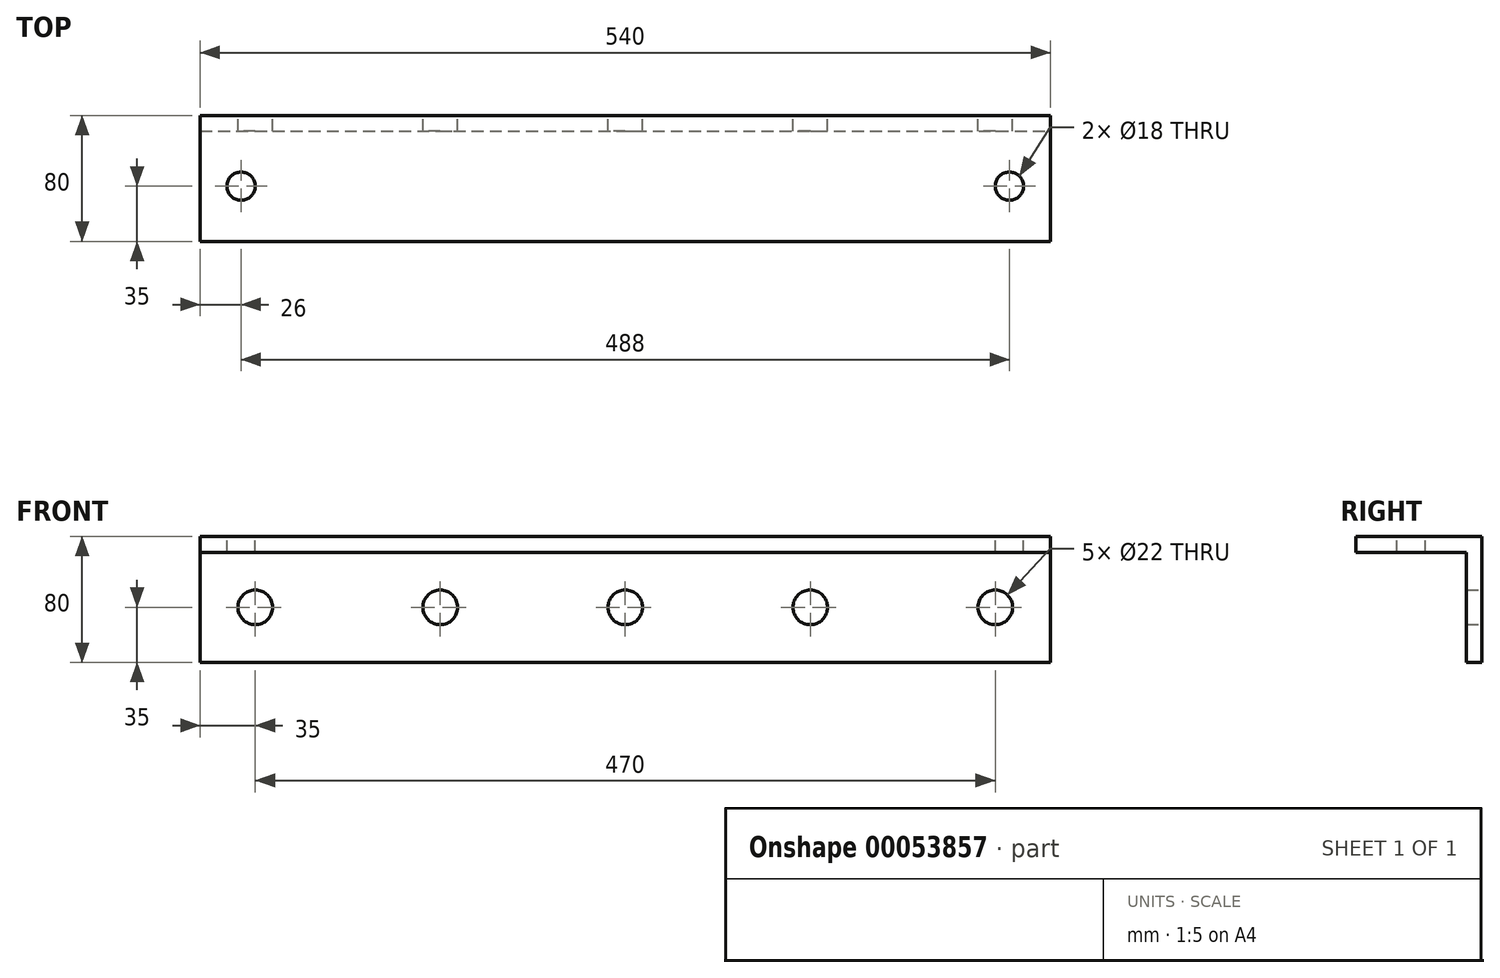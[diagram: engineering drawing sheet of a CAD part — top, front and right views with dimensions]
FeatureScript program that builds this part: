
annotation { "Feature Type Name" : "Feature", "Feature Type Description" : "" }
export const myFeature = defineFeature(function(context is Context, id is Id, definition is map)
    precondition{}
    {
        {
            var Q0;
            Q0=qCreatedBy(makeId("Front.planeOp"),FACE);
            var sketch = newSketch(context, id + "F0", { "sketchPlane" : qUnion([Q0])});
            skLineSegment(sketch, "E0.bottom", {"start": v(0, 0) * mm, "end": v(540, 0) * mm});
            skLineSegment(sketch, "E0.top", {"start": v(0, 80) * mm, "end": v(540, 80) * mm});
            skLineSegment(sketch, "E0.left", {"start": v(0, 0) * mm, "end": v(0, 80) * mm});
            skLineSegment(sketch, "E0.right", {"start": v(540, 0) * mm, "end": v(540, 80) * mm});
            skSolve(sketch);
        }
        {
            var Q0;
            Q0=makeQuery(id+"F0.imprint","IMPRINT",FACE,{"disambiguationData":[TD([[makeQuery(id+"F0.imprint","IMPRINT",EDGE,{"derivedFrom":sQuery(id+"F0.wireOp",EDGE,"E0.bottom")}),1.0]])]});
            extrude(context, id + "F1", {"entities" : qUnion([Q0]), "depth" : 10 * mm});
        }
        {
            var Q0;
            Q0=makeQuery(id+"F1.opExtrude","CAP_FACE",FACE,{"disambiguationData":[OSD([sQuery(id+"F0.wireOp",EDGE,"E0.bottom"),sQuery(id+"F0.wireOp",EDGE,"E0.top"),sQuery(id+"F0.wireOp",EDGE,"E0.left"),sQuery(id+"F0.wireOp",EDGE,"E0.right")])],"isStart":false});
            var sketch = newSketch(context, id + "F2", { "sketchPlane" : qUnion([Q0])});
            skLineSegment(sketch, "E1.bottom", {"start": v(0, 80) * mm, "end": v(540, 80) * mm});
            skLineSegment(sketch, "E1.top", {"start": v(0, 70) * mm, "end": v(540, 70) * mm});
            skLineSegment(sketch, "E1.left", {"start": v(0, 80) * mm, "end": v(0, 70) * mm});
            skLineSegment(sketch, "E1.right", {"start": v(540, 80) * mm, "end": v(540, 70) * mm});
            skSolve(sketch);
        }
        {
            var Q0;
            Q0 = qSketchRegion(id + "F2", true);
            extrude(context, id + "F3", {"entities" : qUnion([Q0]), "operationType" : NewBodyOperationType.ADD, "depth" : 70 * mm});
        }
        {
            var Q0;
            Q0=makeQuery(id+"F1.opExtrude","CAP_FACE",FACE,{"disambiguationData":[OSD([sQuery(id+"F0.wireOp",EDGE,"E0.bottom"),sQuery(id+"F0.wireOp",EDGE,"E0.top"),sQuery(id+"F0.wireOp",EDGE,"E0.left"),sQuery(id+"F0.wireOp",EDGE,"E0.right")])],"isStart":true});
            var sketch = newSketch(context, id + "F4", { "sketchPlane" : qUnion([Q0])});
            skCircle(sketch, "E2", {"center": v(-505, 35) * mm, "radius": 11 * mm});
            skCircle(sketch, "E3", {"center": v(-387.5, 35) * mm, "radius": 11 * mm});
            skCircle(sketch, "E4", {"center": v(-270, 35) * mm, "radius": 11 * mm});
            skCircle(sketch, "E5", {"center": v(-152.5, 35) * mm, "radius": 11 * mm});
            skCircle(sketch, "E6", {"center": v(-35, 35) * mm, "radius": 11 * mm});
            skSolve(sketch);
        }
        {
            var Q0;
            Q0 = qSketchRegion(id + "F4", true);
            extrude(context, id + "F5", {"entities" : qUnion([Q0]), "operationType" : NewBodyOperationType.REMOVE, "endBound" : BoundingType.THROUGH_ALL, "oppositeDirection" : true, "depth" : 25 * mm});
        }
        {
            var Q0;
            Q0=makeQuery(id+"F3.boolean.opBoolean","MERGE",FACE,{"derivedFrom":[makeQuery(id+"F1.opExtrude","SWEPT_FACE",FACE,{"disambiguationData":[OSD([sQuery(id+"F0.wireOp",EDGE,"E0.top")])]}),makeQuery(id+"F3.opExtrude","SWEPT_FACE",FACE,{"disambiguationData":[OSD([sQuery(id+"F2.wireOp",EDGE,"E1.bottom")])]})]});
            var sketch = newSketch(context, id + "F6", { "sketchPlane" : qUnion([Q0])});
            skCircle(sketch, "E7", {"center": v(26, -45) * mm, "radius": 9 * mm});
            skCircle(sketch, "E8", {"center": v(514, -45) * mm, "radius": 9 * mm});
            skSolve(sketch);
        }
        {
            var Q0;
            Q0 = qSketchRegion(id + "F6", true);
            extrude(context, id + "F7", {"entities" : qUnion([Q0]), "operationType" : NewBodyOperationType.REMOVE, "endBound" : BoundingType.THROUGH_ALL, "oppositeDirection" : true, "depth" : 25 * mm});
        }
    });
